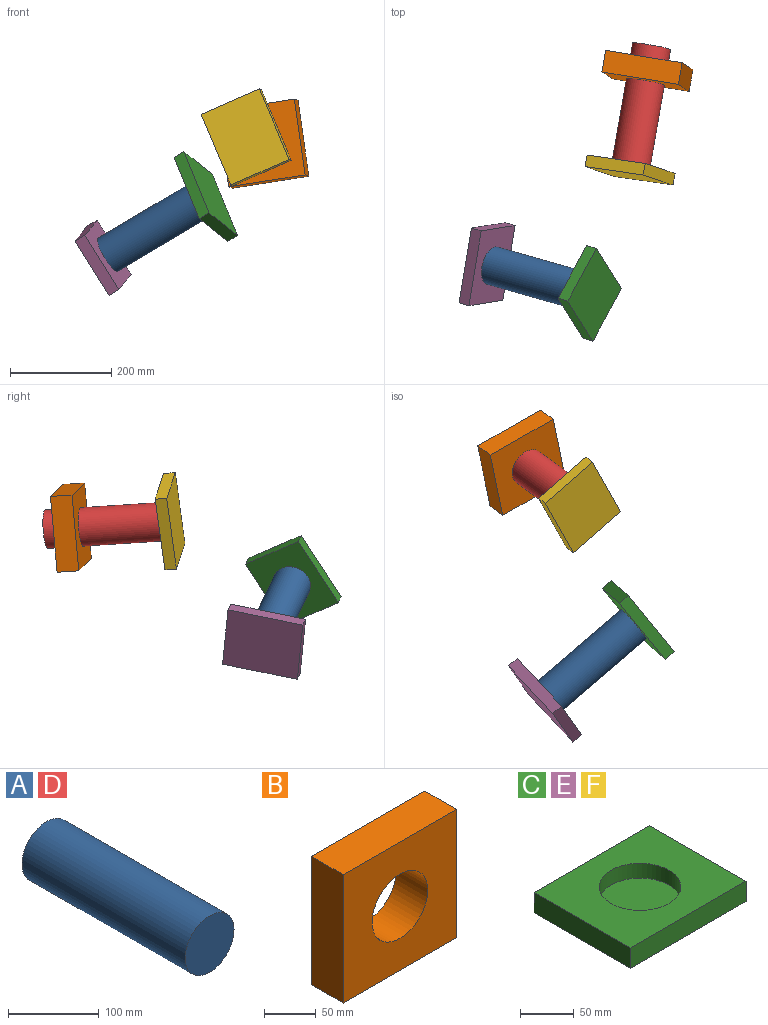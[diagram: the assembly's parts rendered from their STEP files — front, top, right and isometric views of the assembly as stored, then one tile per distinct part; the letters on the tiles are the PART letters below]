
ASSEMBLY  parts=6 mates=4
PART A: 3 faces, bbox 76.2x254x76.2 mm
  f0: cylinder r=38.1mm len=254mm, axis (0,1,0), area 60804.9mm2, adj f1,f2
  f1: plane 76.2x76.2mm, normal (0,-1,0), area 4560.4mm2, adj f0
  f2: plane 76.2x76.2mm, normal (0,1,0), area 4560.4mm2, adj f0
PART B: 7 faces, bbox 154.9x43.5x152 mm
  f0: plane 152.01x43.5mm, normal (1,0,0), area 6612.6mm2, adj f1,f3,f4,f5
  f1: plane 154.95x152.01mm, normal (0,1,0), area 18993.2mm2, adj f0,f2,f4,f5,f6
  f2: plane 152.01x43.5mm, normal (-1,0,0), area 6612.6mm2, adj f1,f3,f4,f5
  f3: plane 154.95x152.01mm, normal (0,-1,0), area 18993.2mm2, adj f0,f2,f4,f5,f6
  f4: plane 154.95x43.5mm, normal (0,0,1), area 6740.3mm2, adj f0,f1,f2,f3
  f5: plane 154.95x43.5mm, normal (0,0,-1), area 6740.3mm2, adj f0,f1,f2,f3
  f6: cylinder r=38.1mm len=76.2mm, axis (0,-1,0), area 10413.6mm2, adj f1,f3
PART C: 8 faces, bbox 152.9x126.9x23.2 mm
  f0: plane 126.91x23.2mm, normal (1,0,0), area 2944.3mm2, adj f1,f3,f4,f5
  f1: plane 152.87x126.91mm, normal (0,0,1), area 14840.4mm2, adj f0,f2,f4,f5,f6
  f2: plane 126.91x23.2mm, normal (-1,0,0), area 2944.3mm2, adj f1,f3,f4,f5
  f3: plane 152.87x126.91mm, normal (0,0,-1), area 19400.8mm2, adj f0,f2,f4,f5
  f4: plane 152.87x23.2mm, normal (0,-1,0), area 3546.8mm2, adj f0,f1,f2,f3
  f5: plane 152.87x23.2mm, normal (0,1,0), area 3546.8mm2, adj f0,f1,f2,f3
  f6: cylinder r=38.1mm len=76.2mm, axis (0,0,1), area 4047.4mm2, adj f1,f7
  f7: plane 76.2x76.2mm, normal (0,0,1), area 4560.4mm2, adj f6
PART D: same geometry as A
PART E: same geometry as C
PART F: same geometry as C
PLACE A rot(axis=(-0.67,0.29,0.68),80.4deg) t=(-240.11,-77.71,139.85)mm
PLACE B rot(axis=(-0.32,-0.63,-0.71),13.5deg) t=(-24.64,333.34,304.91)mm
PLACE C rot(axis=(-0.34,-0.94,0.04),120deg) t=(-138.58,-106.64,200.39)mm
PLACE D rot(axis=(-0.32,-0.63,-0.71),13.5deg) t=(-37.99,256.8,309.84)mm
PLACE E rot(axis=(-0.32,0.54,-0.78),106.7deg) t=(-341.64,-48.78,79.32)mm
PLACE F rot(axis=(-0.72,0.56,0.41),105.8deg) t=(-58.86,137.16,317.55)mm
MATE revolute F.f6 <-> D.f0  axis (0.17,0.98,-0.06) through (-59.77,131.94,317.89)mm
MATE revolute A.f0 <-> E.f6  axis (-0.83,0.24,-0.5) through (-346.06,-47.51,76.68)mm
MATE slider D.f0 <-> B.f6  axis (0.17,0.98,-0.06) through (-16.22,381.66,301.8)mm
MATE revolute C.f6 <-> A.f0  axis (-0.83,0.24,-0.5) through (-134.16,-107.9,203.03)mm
